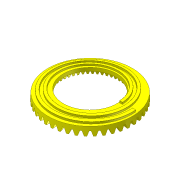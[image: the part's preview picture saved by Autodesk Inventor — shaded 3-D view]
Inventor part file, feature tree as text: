
AUTODESK INVENTOR PART (.ipt)
format: ipt  version: unknown  size: 588,800 bytes
history: native  units: in
note: dims shown in document units (in); Inventor stores cm internally (conversion verified against a paired STEP export)
features: sketch x5, plane x3, other x2, fillet x2, revolve x1, helix x1, extrude x1, loft x1, pattern_circular x1
ambient origin geometry x8: Origin, YZ Plane, XZ Plane, XY Plane, X Axis, Y Axis, Z Axis, Center Point
feature tree (17):
  revolve  "Revolution3"  [1 undecoded]
  other  "Work Point1"
  plane  "Work Plane7"
  sketch  "Sketch12"  dims[d90=0.065in d91=0.2756in d92=0.0394in d96=0.0492in]
  helix  "Coil1"  [1 undecoded]
  extrude  "Extrusion8"  Depth=0.2756in
  other  "Work Axis1"
  fillet  "Fillet3"  Radius=0.0394in
  fillet  "Fillet4"  Radius=0.0492in
  plane  "Work Plane9"
  loft  "Loft1"
  pattern_circular  "Circular Pattern3"  [2 undecoded]
  sketch  "Sketch1"  dims[d1=0.1825in d88=0.1575in d89=0.0852in]
  sketch  "Sketch13"  dims[d97=0.2756in d98=0.1969in]
  sketch  "Sketch14"  dims[d99=90.0deg]
  plane  "Work Plane8"
  sketch  "Sketch15"  dims[d101=0.9449in d102=0.1575in d103=1.8898in d104=0.6299in d105=0.0591in d106=0.0394in d107=0.1181in d108=0.3937in d109=0.7874in d110=0.0in d111=90.0deg d112=90.0deg d113=0.0in d114=0.0in d115=1.1811in d116=0.3937in d117=0.0in d118=0.002in d119=0.002in d120=0.9579in d121=0.5534in d122=0.9646in d123=0.0394in d124=0.0886in d125=0.1374in d126=0.0309in d127=0.0079in d128=0.0in d129=90.0deg d130=0.0in d131=90.0deg d132=18.8976in d133=360.0deg]
note: 4 required parameter values undecoded (feature->parameter linkage not recoverable at this tier; creation-order binding heuristic only, values carry confidence <= 0.55)